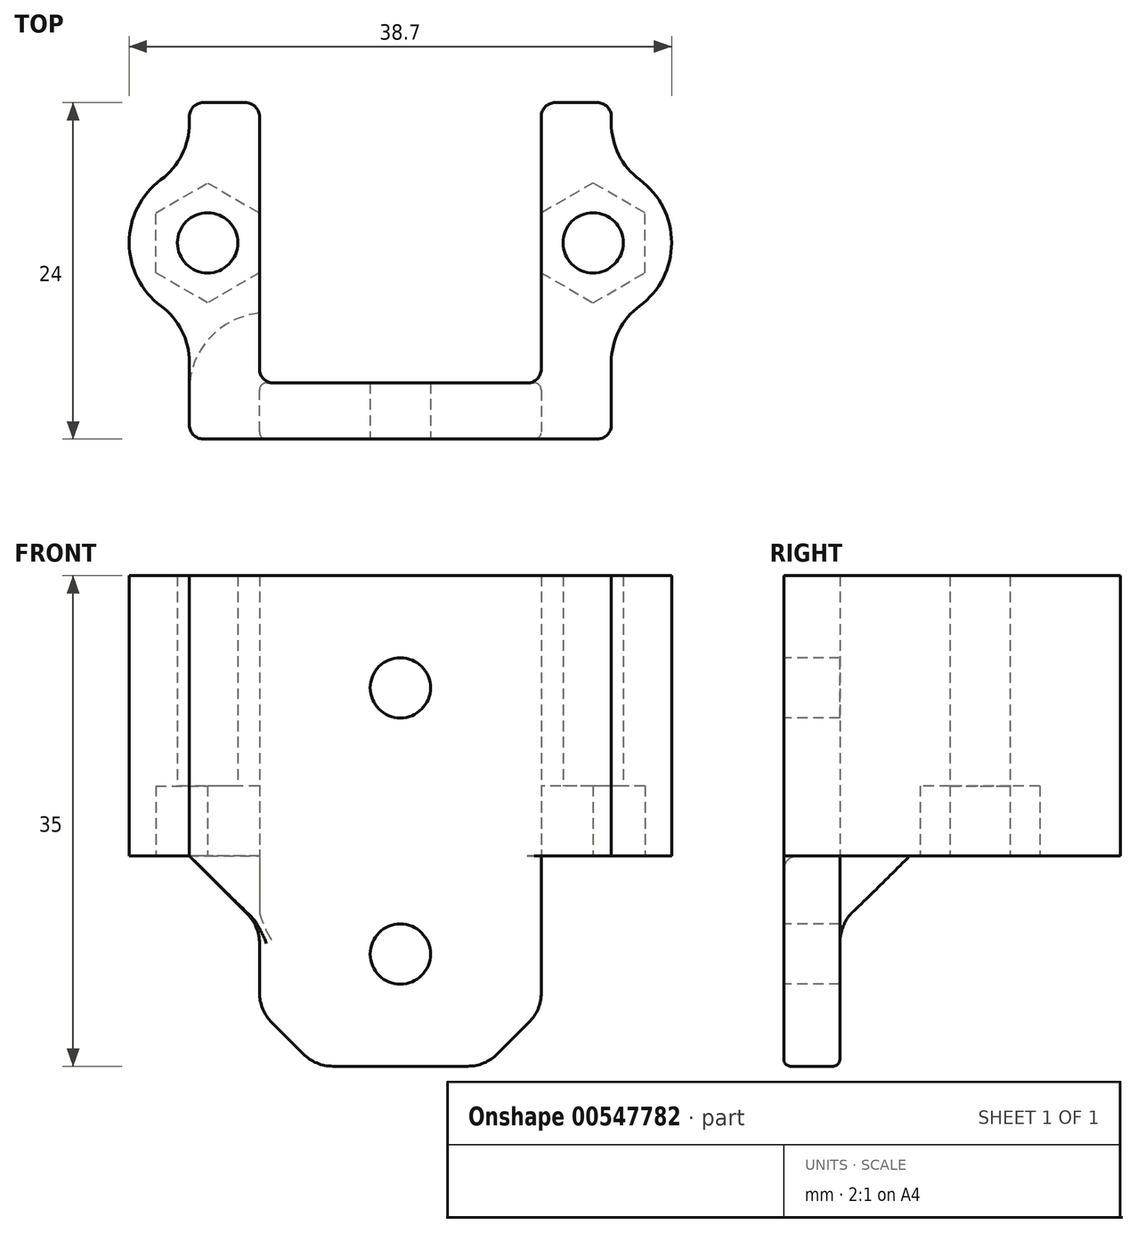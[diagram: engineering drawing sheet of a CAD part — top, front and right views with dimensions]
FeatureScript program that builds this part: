
annotation { "Feature Type Name" : "Feature", "Feature Type Description" : "" }
export const myFeature = defineFeature(function(context is Context, id is Id, definition is map)
    precondition{}
    {
        {
            var Q0;
            Q0=qCreatedBy(makeId("Top.planeOp"),FACE);
            var sketch = newSketch(context, id + "F0", { "sketchPlane" : qUnion([Q0])});
            skLineSegment(sketch, "E0.bottom", {"start": v(10.05, -10) * mm, "end": v(-10.05, -10) * mm, "construction": true});
            skLineSegment(sketch, "E0.top", {"start": v(10.05, 10) * mm, "end": v(-10.05, 10) * mm, "construction": true});
            skLineSegment(sketch, "E0.left", {"start": v(10.05, -10) * mm, "end": v(10.05, 10) * mm, "construction": true});
            skLineSegment(sketch, "E0.right", {"start": v(-10.05, -10) * mm, "end": v(-10.05, 10) * mm, "construction": true});
            skPoint(sketch, "E0.middle", {"position": v(0, 0) * mm});
            skLineSegment(sketch, "E1", {"start": v(-11.05, 10) * mm, "end": v(-14.05, 10) * mm});
            skLineSegment(sketch, "E2", {"start": v(-15.05, 9) * mm, "end": v(-15.05, -13) * mm});
            skLineSegment(sketch, "E3", {"start": v(-14.05, -14) * mm, "end": v(14.05, -14) * mm});
            skLineSegment(sketch, "E4", {"start": v(15.05, -13) * mm, "end": v(15.05, 9) * mm});
            skLineSegment(sketch, "E5", {"start": v(14.05, 10) * mm, "end": v(11.05, 10) * mm});
            skLineSegment(sketch, "E6", {"start": v(10.05, -9) * mm, "end": v(10.05, 9) * mm});
            skLineSegment(sketch, "E7", {"start": v(9.05, -10) * mm, "end": v(-9.05, -10) * mm});
            skLineSegment(sketch, "E8", {"start": v(-10.05, -9) * mm, "end": v(-10.05, 9) * mm});
            skLineSegment(sketch, "E9", {"start": v(-22.03, 0) * mm, "end": v(35.78, 0) * mm, "construction": true});
            skPoint(sketch, "E10.visualSharp", {"position": v(-15.05, -14) * mm});
            skArc(sketch, "E10.filletArc", {"start": v(-15.05, -13) * mm, "mid": v(-14.76, -13.7) * mm, "end": v(-14.05, -14) * mm});
            skPoint(sketch, "E11.visualSharp", {"position": v(15.05, -14) * mm});
            skArc(sketch, "E11.filletArc", {"start": v(14.05, -14) * mm, "mid": v(14.76, -13.7) * mm, "end": v(15.05, -13) * mm});
            skPoint(sketch, "E12.visualSharp", {"position": v(10.05, -10) * mm});
            skArc(sketch, "E12.filletArc", {"start": v(9.05, -10) * mm, "mid": v(9.76, -9.7) * mm, "end": v(10.05, -9) * mm});
            skPoint(sketch, "E13.visualSharp", {"position": v(-10.05, -10) * mm});
            skArc(sketch, "E13.filletArc", {"start": v(-10.05, -9) * mm, "mid": v(-9.76, -9.7) * mm, "end": v(-9.05, -10) * mm});
            skCircle(sketch, "E14", {"center": v(-13.75, 0) * mm, "radius": 2.15 * mm});
            skArc(sketch, "E15", {"start": v(-15.05, 5.45) * mm, "mid": v(-19.35, 0) * mm, "end": v(-15.05, -5.45) * mm});
            skCircle(sketch, "E16.MirrorC", {"center": v(13.75, 0) * mm, "radius": 2.15 * mm});
            skArc(sketch, "E17.MirrorCS", {"start": v(15.05, 5.45) * mm, "mid": v(19.35, 0) * mm, "end": v(15.05, -5.45) * mm});
            skPoint(sketch, "E18.visualSharp", {"position": v(-10.05, 10) * mm});
            skArc(sketch, "E18.filletArc", {"start": v(-10.05, 9) * mm, "mid": v(-10.34, 9.7) * mm, "end": v(-11.05, 10) * mm});
            skPoint(sketch, "E19.visualSharp", {"position": v(-15.05, 10) * mm});
            skArc(sketch, "E19.filletArc", {"start": v(-14.05, 10) * mm, "mid": v(-14.76, 9.7) * mm, "end": v(-15.05, 9) * mm});
            skPoint(sketch, "E20.visualSharp", {"position": v(10.05, 10) * mm});
            skArc(sketch, "E20.filletArc", {"start": v(11.05, 10) * mm, "mid": v(10.34, 9.7) * mm, "end": v(10.05, 9) * mm});
            skPoint(sketch, "E21.visualSharp", {"position": v(15.05, 10) * mm});
            skArc(sketch, "E21.filletArc", {"start": v(15.05, 9) * mm, "mid": v(14.76, 9.7) * mm, "end": v(14.05, 10) * mm});
            skCircle(sketch, "E22.cCircle", {"center": v(-13.75, 0) * mm, "radius": 3.7 * mm, "construction": true});
            skLineSegment(sketch, "E22.0", {"start": v(-10.05, -2.14) * mm, "end": v(-13.75, -4.27) * mm});
            skLineSegment(sketch, "E22.1", {"start": v(-13.75, -4.27) * mm, "end": v(-17.45, -2.14) * mm});
            skLineSegment(sketch, "E22.2", {"start": v(-17.45, -2.14) * mm, "end": v(-17.45, 2.14) * mm});
            skLineSegment(sketch, "E22.3", {"start": v(-17.45, 2.14) * mm, "end": v(-13.75, 4.27) * mm});
            skLineSegment(sketch, "E22.4", {"start": v(-13.75, 4.27) * mm, "end": v(-10.05, 2.14) * mm});
            skLineSegment(sketch, "E22.5", {"start": v(-10.05, 2.14) * mm, "end": v(-10.05, -2.14) * mm});
            skPoint(sketch, "E22.0.midPoint", {"position": v(-11.9, -3.2) * mm});
            skCircle(sketch, "E23.MirrorC", {"center": v(13.75, 0) * mm, "radius": 3.7 * mm, "construction": true});
            skLineSegment(sketch, "E24.MirrorCS", {"start": v(13.75, 4.27) * mm, "end": v(10.05, 2.14) * mm});
            skLineSegment(sketch, "E25.MirrorCS", {"start": v(17.45, 2.14) * mm, "end": v(13.75, 4.27) * mm});
            skLineSegment(sketch, "E26.MirrorCS", {"start": v(17.45, -2.14) * mm, "end": v(17.45, 2.14) * mm});
            skLineSegment(sketch, "E27.MirrorCS", {"start": v(13.75, -4.27) * mm, "end": v(17.45, -2.14) * mm});
            skLineSegment(sketch, "E28.MirrorCS", {"start": v(10.05, -2.14) * mm, "end": v(13.75, -4.27) * mm});
            skLineSegment(sketch, "E29.MirrorCS", {"start": v(10.05, 2.14) * mm, "end": v(10.05, -2.14) * mm});
            skSolve(sketch);
        }
        {
            var Q0;
            Q0=qSketchRegion(id+"F0",true);
            var Q1;
            {var subQ6=sQuery(id+"F0.wireOp",EDGE,"E22.2");Q1=makeQuery(id+"F0.imprint","IMPRINT",FACE,{"disambiguationData":[TD([[makeQuery(id+"F0.imprint","IMPRINT",EDGE,{"derivedFrom":subQ6}),-1.0]])]});}
            var Q2;
            {var subQ0=sQuery(id+"F0.wireOp",EDGE,"E26.MirrorCS");Q2=makeQuery(id+"F0.imprint","IMPRINT",FACE,{"disambiguationData":[TD([[makeQuery(id+"F0.imprint","IMPRINT",EDGE,{"derivedFrom":subQ0}),1.0]])]});}
            extrude(context, id + "F1", {"entities" : qUnion([Q0, Q1, Q2]), "depth" : 20 * mm});
        }
        {
            var Q0;
            {var subQ0=sQuery(id+"F0.wireOp",EDGE,"E24.MirrorCS");Q0=makeQuery(id+"F0.imprint","IMPRINT",FACE,{"disambiguationData":[TD([[makeQuery(id+"F0.imprint","IMPRINT",EDGE,{"derivedFrom":subQ0}),1.0]])]});}
            var Q1;
            {var subQ0=sQuery(id+"F0.wireOp",EDGE,"E26.MirrorCS");Q1=makeQuery(id+"F0.imprint","IMPRINT",FACE,{"disambiguationData":[TD([[makeQuery(id+"F0.imprint","IMPRINT",EDGE,{"derivedFrom":subQ0}),1.0]])]});}
            var Q2;
            {var subQ0=sQuery(id+"F0.wireOp",EDGE,"E22.0");Q2=makeQuery(id+"F0.imprint","IMPRINT",FACE,{"disambiguationData":[TD([[makeQuery(id+"F0.imprint","IMPRINT",EDGE,{"derivedFrom":subQ0}),-1.0]])]});}
            var Q3;
            {var subQ6=sQuery(id+"F0.wireOp",EDGE,"E22.2");Q3=makeQuery(id+"F0.imprint","IMPRINT",FACE,{"disambiguationData":[TD([[makeQuery(id+"F0.imprint","IMPRINT",EDGE,{"derivedFrom":subQ6}),-1.0]])]});}
            extrude(context, id + "F2", {"entities" : qUnion([Q0, Q1, Q2, Q3]), "operationType" : NewBodyOperationType.REMOVE, "depth" : 5 * mm});
        }
        {
            var Q0;
            Q0=makeQuery(id+"F1.opExtrude","CAP_FACE",FACE,{"disambiguationData":[OSD([sQuery(id+"F0.wireOp",EDGE,"E1"),sQuery(id+"F0.wireOp",EDGE,"E2"),sQuery(id+"F0.wireOp",EDGE,"E3"),sQuery(id+"F0.wireOp",EDGE,"E4"),sQuery(id+"F0.wireOp",EDGE,"E5"),sQuery(id+"F0.wireOp",EDGE,"E6"),sQuery(id+"F0.wireOp",EDGE,"E7"),sQuery(id+"F0.wireOp",EDGE,"E8"),sQuery(id+"F0.wireOp",EDGE,"E10.filletArc"),sQuery(id+"F0.wireOp",EDGE,"E11.filletArc"),sQuery(id+"F0.wireOp",EDGE,"E12.filletArc"),sQuery(id+"F0.wireOp",EDGE,"E13.filletArc"),sQuery(id+"F0.wireOp",EDGE,"E14"),sQuery(id+"F0.wireOp",EDGE,"E15"),sQuery(id+"F0.wireOp",EDGE,"E16.MirrorC"),sQuery(id+"F0.wireOp",EDGE,"E17.MirrorCS"),sQuery(id+"F0.wireOp",EDGE,"E18.filletArc"),sQuery(id+"F0.wireOp",EDGE,"E19.filletArc"),sQuery(id+"F0.wireOp",EDGE,"E20.filletArc"),sQuery(id+"F0.wireOp",EDGE,"E21.filletArc"),sQuery(id+"F0.wireOp",EDGE,"E22.5"),sQuery(id+"F0.wireOp",EDGE,"E29.MirrorCS")])],"isStart":true});
            var sketch = newSketch(context, id + "F3", { "sketchPlane" : qUnion([Q0])});
            skLineSegment(sketch, "E30", {"start": v(15.05, 10) * mm, "end": v(-15.05, 10) * mm});
            skLineSegment(sketch, "E31", {"start": v(10.05, 9) * mm, "end": v(10.05, 14) * mm});
            skLineSegment(sketch, "E32", {"start": v(-10.05, 9) * mm, "end": v(-10.05, 14) * mm});
            skSolve(sketch);
        }
        {
            var Q0;
            {var subQ0=sQuery(id+"F3.wireOp",EDGE,"E30");var subQ4=makeQuery(id+"F3.imprint","INTERSECT",VERTEX,{"derivedFrom":[makeQuery(id+"F1.opExtrude","CAP_EDGE",EDGE,{"disambiguationData":[OSD([sQuery(id+"F0.wireOp",EDGE,"E12.filletArc")])],"isStart":true}),subQ0]});Q0=makeQuery(id+"F3.imprint","IMPRINT",FACE,{"disambiguationData":[TD([[makeQuery(id+"F3.imprint","IMPRINT",EDGE,{"disambiguationData":[TD([[subQ4,1.0]])],"derivedFrom":subQ0}),-1.0]])]});}
            extrude(context, id + "F4", {"entities" : qUnion([Q0]), "operationType" : NewBodyOperationType.ADD, "depth" : 15 * mm});
        }
        {
            var Q0;
            Q0=makeQuery(id+"F1.opExtrude","SWEPT_FACE",FACE,{"disambiguationData":[OSD([sQuery(id+"F0.wireOp",EDGE,"E3")])]});
            var sketch = newSketch(context, id + "F5", { "sketchPlane" : qUnion([Q0])});
            skPoint(sketch, "E33.centerSnap0", {"position": v(-14.05, 10) * mm});
            skCircle(sketch, "E34", {"center": v(0, -7) * mm, "radius": 2.15 * mm});
            skCircle(sketch, "E35", {"center": v(0, 12) * mm, "radius": 2.15 * mm});
            skSolve(sketch);
        }
        {
            var Q0;
            Q0=makeQuery(id+"F5.imprint","IMPRINT",FACE,{"disambiguationData":[TD([[makeQuery(id+"F5.imprint","IMPRINT",EDGE,{"derivedFrom":sQuery(id+"F5.wireOp",EDGE,"E35")}),1.0]])]});
            var Q1;
            Q1=makeQuery(id+"F5.imprint","IMPRINT",FACE,{"disambiguationData":[TD([[makeQuery(id+"F5.imprint","IMPRINT",EDGE,{"derivedFrom":sQuery(id+"F5.wireOp",EDGE,"E34")}),1.0]])]});
            extrude(context, id + "F6", {"entities" : qUnion([Q0, Q1]), "operationType" : NewBodyOperationType.REMOVE, "endBound" : BoundingType.THROUGH_ALL, "oppositeDirection" : true, "depth" : 25 * mm});
        }
        {
            var Q0;
            Q0=makeQuery(id+"F4.opExtrude","CAP_EDGE",EDGE,{"disambiguationData":[OSD([sQuery(id+"F3.wireOp",EDGE,"E32")])],"isStart":false});
            var Q1;
            Q1=makeQuery(id+"F4.opExtrude","CAP_EDGE",EDGE,{"disambiguationData":[OSD([sQuery(id+"F3.wireOp",EDGE,"E31")])],"isStart":false});
            chamfer(context, id + "F7", {"entities" : qUnion([Q0, Q1]), "width" : 4 * mm, "tangentPropagation" : true});
        }
        {
            var Q0;
            {var subQ0=sQuery(id+"F0.wireOp",EDGE,"E15");var subQ1=sQuery(id+"F0.wireOp",EDGE,"E2");Q0=makeQuery(id+"F1.opExtrude","SWEPT_EDGE",EDGE,{"disambiguationData":[OSD([subQ1,subQ0]),TDD([makeQuery(id+"F0.imprint","INTERSECT",VERTEX,{"disambiguationData":[OD(0.0)],"derivedFrom":[subQ1,subQ0]})])]});}
            var Q1;
            {var subQ0=sQuery(id+"F0.wireOp",EDGE,"E15");var subQ1=sQuery(id+"F0.wireOp",EDGE,"E2");Q1=makeQuery(id+"F1.opExtrude","SWEPT_EDGE",EDGE,{"disambiguationData":[OSD([subQ1,subQ0]),TDD([makeQuery(id+"F0.imprint","INTERSECT",VERTEX,{"disambiguationData":[OD(1.0)],"derivedFrom":[subQ1,subQ0]})])]});}
            var Q2;
            {var subQ0=sQuery(id+"F0.wireOp",EDGE,"E17.MirrorCS");var subQ1=sQuery(id+"F0.wireOp",EDGE,"E4");Q2=makeQuery(id+"F1.opExtrude","SWEPT_EDGE",EDGE,{"disambiguationData":[OSD([subQ1,subQ0]),TDD([makeQuery(id+"F0.imprint","INTERSECT",VERTEX,{"disambiguationData":[OD(1.0)],"derivedFrom":[subQ1,subQ0]})])]});}
            var Q3;
            {var subQ0=sQuery(id+"F0.wireOp",EDGE,"E17.MirrorCS");var subQ1=sQuery(id+"F0.wireOp",EDGE,"E4");Q3=makeQuery(id+"F1.opExtrude","SWEPT_EDGE",EDGE,{"disambiguationData":[OSD([subQ1,subQ0]),TDD([makeQuery(id+"F0.imprint","INTERSECT",VERTEX,{"disambiguationData":[OD(0.0)],"derivedFrom":[subQ1,subQ0]})])]});}
            fillet(context, id + "F8", {"entities" : qUnion([Q0, Q1, Q2, Q3]), "radius" : 5 * mm, "tangentPropagation" : true, "allowEdgeOverflow" : false});
        }
        {
            var Q0;
            Q0=makeQuery(id+"F4.opExtrude","SWEPT_EDGE",EDGE,{"disambiguationData":[OSD([sQuery(id+"F0.wireOp",EDGE,"E3"),sQuery(id+"F3.wireOp",EDGE,"E32")])]});
            var Q1;
            Q1=makeQuery(id+"F4.opExtrude","SWEPT_EDGE",EDGE,{"disambiguationData":[OSD([sQuery(id+"F0.wireOp",EDGE,"E3"),sQuery(id+"F3.wireOp",EDGE,"E31")])]});
            var Q2;
            Q2=makeQuery(id+"F4.opExtrude","SWEPT_EDGE",EDGE,{"disambiguationData":[OSD([sQuery(id+"F3.wireOp",EDGE,"E30"),sQuery(id+"F3.wireOp",EDGE,"E32")])]});
            var Q3;
            Q3=makeQuery(id+"F4.opExtrude","SWEPT_EDGE",EDGE,{"disambiguationData":[OSD([sQuery(id+"F3.wireOp",EDGE,"E30"),sQuery(id+"F3.wireOp",EDGE,"E31")])]});
            var Q4;
            {var subQ0=sQuery(id+"F0.wireOp",EDGE,"E3");Q4=makeQuery(id+"F7.opChamfer","BLEND_EDGE",EDGE,{"blendedFrom":[makeQuery(id+"F4.opExtrude","CAP_EDGE",EDGE,{"disambiguationData":[OSD([sQuery(id+"F3.wireOp",EDGE,"E32")])],"isStart":false}),makeQuery(id+"F4.boolean.opBoolean","MERGE",FACE,{"derivedFrom":[makeQuery(id+"F1.opExtrude","SWEPT_FACE",FACE,{"disambiguationData":[OSD([subQ0])]}),makeQuery(id+"F4.opExtrude","SWEPT_FACE",FACE,{"disambiguationData":[OSD([subQ0])]})]})],"blendedInto":[makeQuery(id+"F4.boolean.opBoolean","MERGE",FACE,{"derivedFrom":[makeQuery(id+"F1.opExtrude","SWEPT_FACE",FACE,{"disambiguationData":[OSD([subQ0])]}),makeQuery(id+"F4.opExtrude","SWEPT_FACE",FACE,{"disambiguationData":[OSD([subQ0])]})]})]});}
            var Q5;
            Q5=makeQuery(id+"F4.opExtrude","CAP_EDGE",EDGE,{"disambiguationData":[OSD([sQuery(id+"F0.wireOp",EDGE,"E3")])],"isStart":false});
            var Q6;
            {var subQ0=sQuery(id+"F0.wireOp",EDGE,"E3");Q6=makeQuery(id+"F7.opChamfer","BLEND_EDGE",EDGE,{"blendedFrom":[makeQuery(id+"F4.opExtrude","CAP_EDGE",EDGE,{"disambiguationData":[OSD([sQuery(id+"F3.wireOp",EDGE,"E31")])],"isStart":false}),makeQuery(id+"F4.boolean.opBoolean","MERGE",FACE,{"derivedFrom":[makeQuery(id+"F1.opExtrude","SWEPT_FACE",FACE,{"disambiguationData":[OSD([subQ0])]}),makeQuery(id+"F4.opExtrude","SWEPT_FACE",FACE,{"disambiguationData":[OSD([subQ0])]})]})],"blendedInto":[makeQuery(id+"F4.boolean.opBoolean","MERGE",FACE,{"derivedFrom":[makeQuery(id+"F1.opExtrude","SWEPT_FACE",FACE,{"disambiguationData":[OSD([subQ0])]}),makeQuery(id+"F4.opExtrude","SWEPT_FACE",FACE,{"disambiguationData":[OSD([subQ0])]})]})]});}
            var Q7;
            Q7=makeQuery(id+"F7.opChamfer","BLEND_EDGE",EDGE,{"blendedFrom":[makeQuery(id+"F4.opExtrude","CAP_EDGE",EDGE,{"disambiguationData":[OSD([sQuery(id+"F3.wireOp",EDGE,"E31")])],"isStart":false}),makeQuery(id+"F4.boolean.opBoolean","MERGE",FACE,{"derivedFrom":[makeQuery(id+"F1.opExtrude","SWEPT_FACE",FACE,{"disambiguationData":[OSD([sQuery(id+"F0.wireOp",EDGE,"E7")])]}),makeQuery(id+"F4.opExtrude","SWEPT_FACE",FACE,{"disambiguationData":[OSD([sQuery(id+"F3.wireOp",EDGE,"E30")])]})]})],"blendedInto":[makeQuery(id+"F4.boolean.opBoolean","MERGE",FACE,{"derivedFrom":[makeQuery(id+"F1.opExtrude","SWEPT_FACE",FACE,{"disambiguationData":[OSD([sQuery(id+"F0.wireOp",EDGE,"E7")])]}),makeQuery(id+"F4.opExtrude","SWEPT_FACE",FACE,{"disambiguationData":[OSD([sQuery(id+"F3.wireOp",EDGE,"E30")])]})]})]});
            var Q8;
            Q8=makeQuery(id+"F4.opExtrude","CAP_EDGE",EDGE,{"disambiguationData":[OSD([sQuery(id+"F3.wireOp",EDGE,"E30")])],"isStart":false});
            var Q9;
            Q9=makeQuery(id+"F7.opChamfer","BLEND_EDGE",EDGE,{"blendedFrom":[makeQuery(id+"F4.opExtrude","CAP_EDGE",EDGE,{"disambiguationData":[OSD([sQuery(id+"F3.wireOp",EDGE,"E32")])],"isStart":false}),makeQuery(id+"F4.boolean.opBoolean","MERGE",FACE,{"derivedFrom":[makeQuery(id+"F1.opExtrude","SWEPT_FACE",FACE,{"disambiguationData":[OSD([sQuery(id+"F0.wireOp",EDGE,"E7")])]}),makeQuery(id+"F4.opExtrude","SWEPT_FACE",FACE,{"disambiguationData":[OSD([sQuery(id+"F3.wireOp",EDGE,"E30")])]})]})],"blendedInto":[makeQuery(id+"F4.boolean.opBoolean","MERGE",FACE,{"derivedFrom":[makeQuery(id+"F1.opExtrude","SWEPT_FACE",FACE,{"disambiguationData":[OSD([sQuery(id+"F0.wireOp",EDGE,"E7")])]}),makeQuery(id+"F4.opExtrude","SWEPT_FACE",FACE,{"disambiguationData":[OSD([sQuery(id+"F3.wireOp",EDGE,"E30")])]})]})]});
            fillet(context, id + "F9", {"entities" : qUnion([Q0, Q1, Q2, Q3, Q4, Q5, Q6, Q7, Q8, Q9]), "radius" : 0.5 * mm, "tangentPropagation" : true, "allowEdgeOverflow" : false});
        }
        {
            var Q0;
            Q0=makeQuery(id+"F4.opExtrude","CAP_EDGE",EDGE,{"disambiguationData":[OSD([sQuery(id+"F3.wireOp",EDGE,"E32")])],"isStart":true});
            var Q1;
            Q1=makeQuery(id+"F4.opExtrude","CAP_EDGE",EDGE,{"disambiguationData":[OSD([sQuery(id+"F3.wireOp",EDGE,"E31")])],"isStart":true});
            chamfer(context, id + "F10", {"entities" : qUnion([Q0, Q1]), "width" : 5 * mm, "tangentPropagation" : true});
        }
        {
            var Q0;
            {var subQ0=sQuery(id+"F3.wireOp",EDGE,"E32");Q0=makeQuery(id+"F10.opChamfer","BLEND_EDGE",EDGE,{"blendedFrom":[makeQuery(id+"F4.opExtrude","CAP_EDGE",EDGE,{"disambiguationData":[OSD([subQ0])],"isStart":true}),makeQuery(id+"F4.opExtrude","SWEPT_FACE",FACE,{"disambiguationData":[OSD([subQ0])]})],"blendedInto":[makeQuery(id+"F4.opExtrude","SWEPT_FACE",FACE,{"disambiguationData":[OSD([subQ0])]})]});}
            var Q1;
            {var subQ0=sQuery(id+"F3.wireOp",EDGE,"E32");Q1=makeQuery(id+"F7.opChamfer","BLEND_EDGE",EDGE,{"blendedFrom":[makeQuery(id+"F4.opExtrude","CAP_EDGE",EDGE,{"disambiguationData":[OSD([subQ0])],"isStart":false}),makeQuery(id+"F4.opExtrude","SWEPT_FACE",FACE,{"disambiguationData":[OSD([subQ0])]})],"blendedInto":[makeQuery(id+"F4.opExtrude","SWEPT_FACE",FACE,{"disambiguationData":[OSD([subQ0])]})]});}
            var Q2;
            {var subQ0=sQuery(id+"F3.wireOp",EDGE,"E32");Q2=makeQuery(id+"F7.opChamfer","BLEND_EDGE",EDGE,{"blendedFrom":[makeQuery(id+"F4.opExtrude","CAP_EDGE",EDGE,{"disambiguationData":[OSD([subQ0])],"isStart":false}),makeQuery(id+"F4.opExtrude","CAP_FACE",FACE,{"disambiguationData":[OSD([sQuery(id+"F0.wireOp",EDGE,"E3"),sQuery(id+"F3.wireOp",EDGE,"E30"),sQuery(id+"F3.wireOp",EDGE,"E31"),subQ0])],"isStart":false})],"blendedInto":[makeQuery(id+"F4.opExtrude","CAP_FACE",FACE,{"disambiguationData":[OSD([sQuery(id+"F0.wireOp",EDGE,"E3"),sQuery(id+"F3.wireOp",EDGE,"E30"),sQuery(id+"F3.wireOp",EDGE,"E31"),subQ0])],"isStart":false})]});}
            var Q3;
            {var subQ0=sQuery(id+"F3.wireOp",EDGE,"E31");Q3=makeQuery(id+"F10.opChamfer","BLEND_EDGE",EDGE,{"blendedFrom":[makeQuery(id+"F4.opExtrude","CAP_EDGE",EDGE,{"disambiguationData":[OSD([subQ0])],"isStart":true}),makeQuery(id+"F4.opExtrude","SWEPT_FACE",FACE,{"disambiguationData":[OSD([subQ0])]})],"blendedInto":[makeQuery(id+"F4.opExtrude","SWEPT_FACE",FACE,{"disambiguationData":[OSD([subQ0])]})]});}
            var Q4;
            {var subQ0=sQuery(id+"F3.wireOp",EDGE,"E31");Q4=makeQuery(id+"F7.opChamfer","BLEND_EDGE",EDGE,{"blendedFrom":[makeQuery(id+"F4.opExtrude","CAP_EDGE",EDGE,{"disambiguationData":[OSD([subQ0])],"isStart":false}),makeQuery(id+"F4.opExtrude","SWEPT_FACE",FACE,{"disambiguationData":[OSD([subQ0])]})],"blendedInto":[makeQuery(id+"F4.opExtrude","SWEPT_FACE",FACE,{"disambiguationData":[OSD([subQ0])]})]});}
            var Q5;
            {var subQ0=sQuery(id+"F3.wireOp",EDGE,"E31");Q5=makeQuery(id+"F7.opChamfer","BLEND_EDGE",EDGE,{"blendedFrom":[makeQuery(id+"F4.opExtrude","CAP_EDGE",EDGE,{"disambiguationData":[OSD([subQ0])],"isStart":false}),makeQuery(id+"F4.opExtrude","CAP_FACE",FACE,{"disambiguationData":[OSD([sQuery(id+"F0.wireOp",EDGE,"E3"),sQuery(id+"F3.wireOp",EDGE,"E30"),subQ0,sQuery(id+"F3.wireOp",EDGE,"E32")])],"isStart":false})],"blendedInto":[makeQuery(id+"F4.opExtrude","CAP_FACE",FACE,{"disambiguationData":[OSD([sQuery(id+"F0.wireOp",EDGE,"E3"),sQuery(id+"F3.wireOp",EDGE,"E30"),subQ0,sQuery(id+"F3.wireOp",EDGE,"E32")])],"isStart":false})]});}
            fillet(context, id + "F11", {"entities" : qUnion([Q0, Q1, Q2, Q3, Q4, Q5]), "radius" : 3 * mm, "tangentPropagation" : true, "allowEdgeOverflow" : false});
        }
    });
